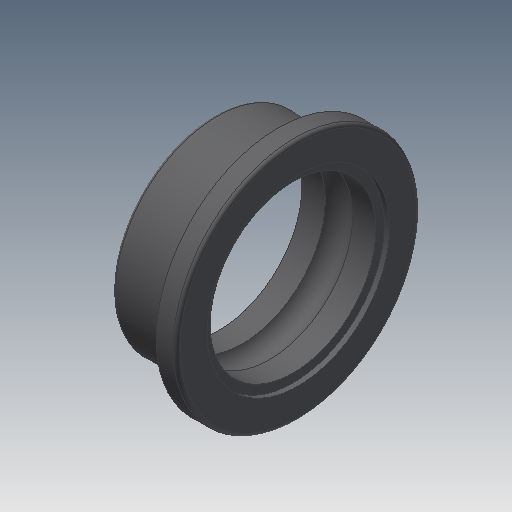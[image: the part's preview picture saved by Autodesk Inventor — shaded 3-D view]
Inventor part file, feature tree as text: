
AUTODESK INVENTOR PART (.ipt)
format: ipt  version: 2019.4 (Build 234330000, 330)  size: 189,952 bytes
history: native  units: mm
features: other x14, revolve x1, sketch x1
ambient origin geometry x8: Origin, YZ Plane, XZ Plane, XY Plane, X Axis, Y Axis, Z Axis, Center Point
bodies: Solid1 (feature_tree)
feature tree (16):
  revolve  "Revolution1"  [1 undecoded]
  other  "ip_st_1_XY"
  other  "ip_st_1_YZ"
  other  "ip_st_1_ZX"
  other  "ip_st_1_X"
  other  "ip_st_1_Y"
  other  "ip_st_1_Z"
  other  "ip_st_1_Center"
  other  "ip_st_2_XY"
  other  "ip_st_2_YZ"
  other  "ip_st_2_ZX"
  other  "ip_st_2_X"
  other  "ip_st_2_Y"
  other  "ip_st_2_Z"
  other  "ip_st_2_Center"
  sketch  "Sketch_1"  dims[d0=360.0deg d1=0.0mm d2=0.0mm]
note: 1 required parameter value undecoded (feature->parameter linkage not recoverable at this tier; creation-order binding heuristic only, values carry confidence <= 0.55)
